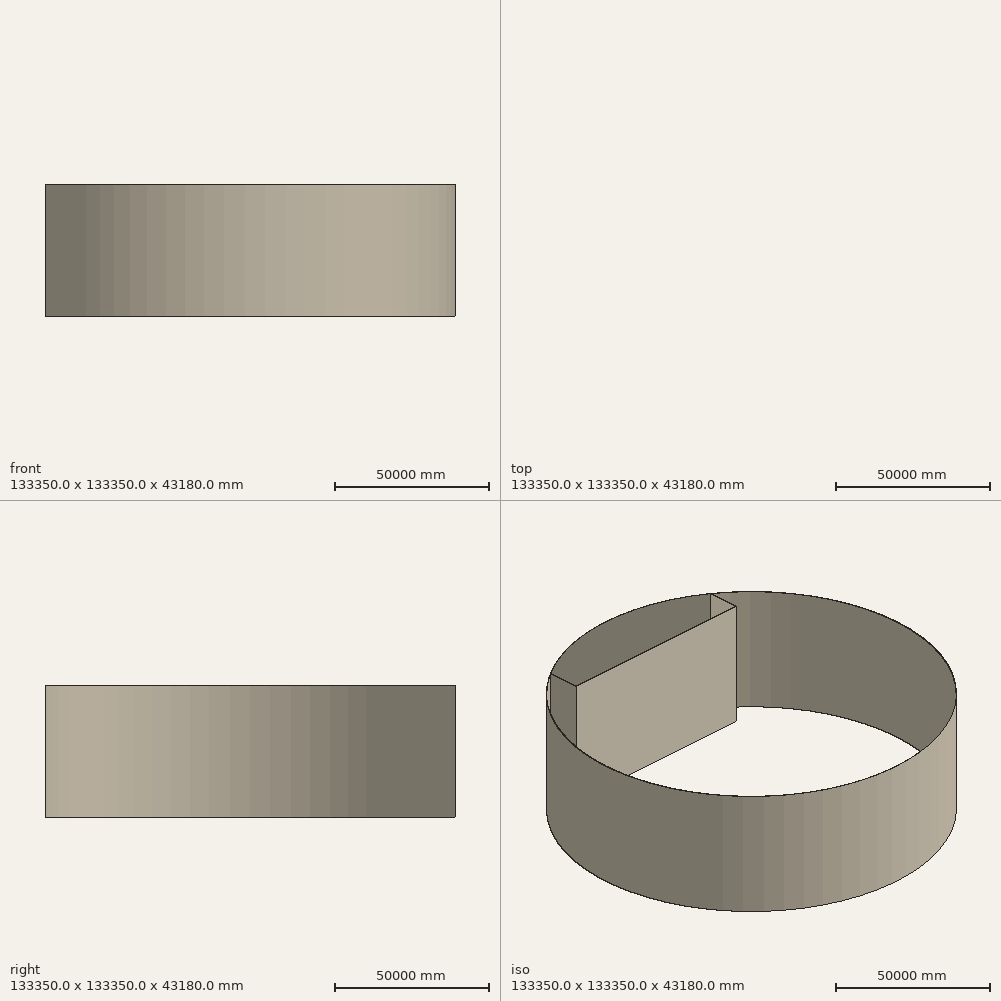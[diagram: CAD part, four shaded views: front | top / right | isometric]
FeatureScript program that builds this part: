
annotation { "Feature Type Name" : "Feature", "Feature Type Description" : "" }
export const myFeature = defineFeature(function(context is Context, id is Id, definition is map)
    precondition{}
    {
        {
            var Q0;
            Q0=qCreatedBy(makeId("Top.planeOp"),FACE);
            var sketch = newSketch(context, id + "F0", { "sketchPlane" : qUnion([Q0])});
            skCircle(sketch, "E0", {"center": v(0, 0) * mm, "radius": 66675 * mm});
            skArc(sketch, "E1", {"start": v(-36830, 55427.32) * mm, "mid": v(0, -66548) * mm, "end": v(36830, 55427.32) * mm});
            skLineSegment(sketch, "E2", {"start": v(0, 113582.34) * mm, "end": v(0, -149085.75) * mm, "construction": true});
            skLineSegment(sketch, "E3", {"start": v(-100020.34, 0) * mm, "end": v(105359.87, 0) * mm, "construction": true});
            skLineSegment(sketch, "E4", {"start": v(-25400, 43688) * mm, "end": v(25400, 43688) * mm});
            skLineSegment(sketch, "E5", {"start": v(25400, 43688) * mm, "end": v(36830, 43688) * mm});
            skLineSegment(sketch, "E6", {"start": v(-25400, 43688) * mm, "end": v(-36830, 43688) * mm});
            skPoint(sketch, "E7.orphan", {"position": v(92293.17, 43688) * mm});
            skLineSegment(sketch, "E8", {"start": v(-36830, 43688) * mm, "end": v(-36830, 55427.32) * mm});
            skLineSegment(sketch, "E9", {"start": v(36830, 43688) * mm, "end": v(36830, 55427.32) * mm});
            skLineSegment(sketch, "E10", {"start": v(-36703, 55511.5) * mm, "end": v(-36703, 43815) * mm});
            skLineSegment(sketch, "E11", {"start": v(-36703, 43815) * mm, "end": v(36703, 43815) * mm});
            skLineSegment(sketch, "E12", {"start": v(36703, 43815) * mm, "end": v(36703, 55511.5) * mm});
            skArc(sketch, "E13.trimOffspring", {"start": v(36703, 55511.5) * mm, "mid": v(0, 66548) * mm, "end": v(-36703, 55511.5) * mm});
            skSolve(sketch);
        }
        {
            var Q0;
            Q0=sQuery(id+"F0.wireOp",EDGE,"E10");
            var Q1;
            Q1=sQuery(id+"F0.wireOp",EDGE,"E8");
            var Q2;
            Q2=sQuery(id+"F0.wireOp",EDGE,"E11");
            var Q3;
            Q3=sQuery(id+"F0.wireOp",EDGE,"E6");
            var Q4;
            Q4=sQuery(id+"F0.wireOp",EDGE,"E12");
            var Q5;
            Q5=sQuery(id+"F0.wireOp",EDGE,"E9");
            var Q6;
            Q6=sQuery(id+"F0.wireOp",EDGE,"E5");
            var Q7;
            Q7=sQuery(id+"F0.wireOp",EDGE,"E4");
            var Q8;
            Q8=sQuery(id+"F0.wireOp",EDGE,"E1");
            var Q9;
            Q9=sQuery(id+"F0.wireOp",EDGE,"E0");
            var Q10;
            Q10=sQuery(id+"F0.wireOp",EDGE,"E13.trimOffspring");
            extrude(context, id + "F1", {"bodyType" : ToolBodyType.SURFACE, "surfaceEntities" : qUnion([Q0, Q1, Q2, Q3, Q4, Q5, Q6, Q7, Q8, Q9, Q10]), "depth" : 43180 * mm, "offsetDistance" : 25.4 * mm});
        }
    });
